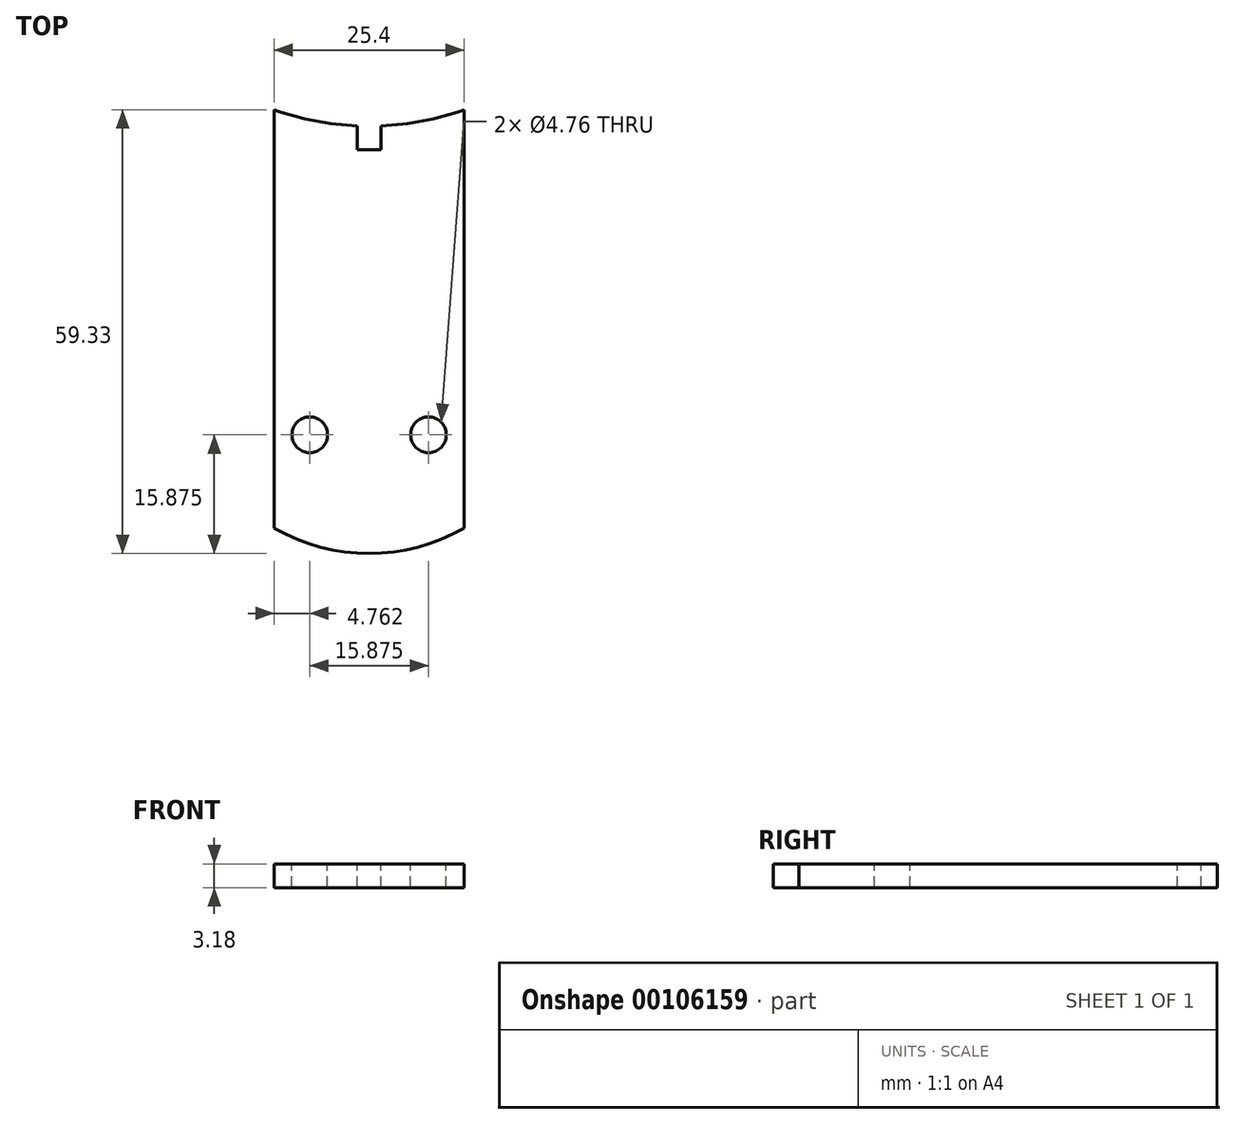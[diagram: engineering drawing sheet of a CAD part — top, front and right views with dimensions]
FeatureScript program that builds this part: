
annotation { "Feature Type Name" : "Feature", "Feature Type Description" : "" }
export const myFeature = defineFeature(function(context is Context, id is Id, definition is map)
    precondition{}
    {
        {
            var Q0;
            Q0=qCreatedBy(makeId("Top.planeOp"),FACE);
            var sketch = newSketch(context, id + "F0", { "sketchPlane" : qUnion([Q0])});
            skLineSegment(sketch, "E0.left", {"start": v(12.7, 47.4) * mm, "end": v(12.7, -47.4) * mm});
            skLineSegment(sketch, "E0.right", {"start": v(-12.7, 47.4) * mm, "end": v(-12.7, -47.4) * mm});
            skPoint(sketch, "E0.middle", {"position": v(0, 0) * mm});
            skLineSegment(sketch, "E1", {"start": v(0, -25.4) * mm, "end": v(0, 25.4) * mm});
            skArc(sketch, "E2", {"start": v(-12.7, -47.4) * mm, "mid": v(0, -50.8) * mm, "end": v(12.7, -47.4) * mm});
            skArc(sketch, "E3.trimOffspring", {"start": v(12.7, 47.4) * mm, "mid": v(0, 50.8) * mm, "end": v(-12.7, 47.4) * mm});
            skPoint(sketch, "E4", {"position": v(0, 50.8) * mm});
            skPoint(sketch, "E5", {"position": v(0, -50.8) * mm});
            skLineSegment(sketch, "E6", {"start": v(-12.7, 0) * mm, "end": v(12.7, 0) * mm});
            skSolve(sketch);
        }
        {
            var Q0;
            Q0=qSketchRegion(id+"F0",true);
            extrude(context, id + "F1", {"entities" : qUnion([Q0]), "depth" : 3.17 * mm});
        }
        {
            var Q0;
            Q0=makeQuery(id+"F1.opExtrude","CAP_FACE",FACE,{"disambiguationData":[OSD([sQuery(id+"F0.wireOp",EDGE,"E0.left"),sQuery(id+"F0.wireOp",EDGE,"E0.right"),sQuery(id+"F0.wireOp",EDGE,"E2"),sQuery(id+"F0.wireOp",EDGE,"E3.trimOffspring")])],"isStart":false});
            var sketch = newSketch(context, id + "F2", { "sketchPlane" : qUnion([Q0])});
            skLineSegment(sketch, "E7.bottom", {"start": v(7.94, 41.27) * mm, "end": v(-7.94, 41.27) * mm, "construction": true});
            skLineSegment(sketch, "E7.top", {"start": v(7.94, -34.92) * mm, "end": v(-7.94, -34.92) * mm, "construction": true});
            skLineSegment(sketch, "E7.left", {"start": v(7.94, 41.27) * mm, "end": v(7.94, -34.92) * mm, "construction": true});
            skLineSegment(sketch, "E7.right", {"start": v(-7.94, 41.27) * mm, "end": v(-7.94, -34.92) * mm, "construction": true});
            skPoint(sketch, "E7.middle", {"position": v(0, 3.18) * mm});
            skCircle(sketch, "E8", {"center": v(-7.94, 41.27) * mm, "radius": 2.38 * mm});
            skCircle(sketch, "E9", {"center": v(7.94, 41.27) * mm, "radius": 2.38 * mm});
            skCircle(sketch, "E10", {"center": v(-7.94, -34.92) * mm, "radius": 2.38 * mm});
            skCircle(sketch, "E11", {"center": v(7.94, -34.92) * mm, "radius": 2.38 * mm});
            skLineSegment(sketch, "E12", {"start": v(0, 0) * mm, "end": v(0, 3.18) * mm});
            skSolve(sketch);
        }
        {
            var Q0;
            Q0=qSketchRegion(id+"F2",true);
            extrude(context, id + "F3", {"entities" : qUnion([Q0]), "operationType" : NewBodyOperationType.REMOVE, "endBound" : BoundingType.UP_TO_NEXT, "oppositeDirection" : true, "depth" : 25.4 * mm});
        }
        {
            var Q0;
            Q0=makeQuery(id+"F1.opExtrude","CAP_FACE",FACE,{"disambiguationData":[OSD([sQuery(id+"F0.wireOp",EDGE,"E0.left"),sQuery(id+"F0.wireOp",EDGE,"E0.right"),sQuery(id+"F0.wireOp",EDGE,"E2"),sQuery(id+"F0.wireOp",EDGE,"E3.trimOffspring")])],"isStart":false});
            var sketch = newSketch(context, id + "F4", { "sketchPlane" : qUnion([Q0])});
            skPoint(sketch, "E13", {"position": v(0, 44.45) * mm});
            skPoint(sketch, "E13.positionSnap0", {"position": v(0, 50.8) * mm});
            skLineSegment(sketch, "E14", {"start": v(0, 0) * mm, "end": v(0, 25.4) * mm, "construction": true});
            skCircle(sketch, "E15", {"center": v(0, 25.4) * mm, "radius": 7.62 * mm, "construction": true});
            skCircle(sketch, "E16", {"center": v(0, 44.45) * mm, "radius": 38.1 * mm});
            skPoint(sketch, "E17", {"position": v(0, 12.7) * mm});
            skLineSegment(sketch, "E18.bottom", {"start": v(-1.59, 6.38) * mm, "end": v(1.59, 6.38) * mm});
            skLineSegment(sketch, "E18.top", {"start": v(-1.59, 3.2) * mm, "end": v(1.59, 3.2) * mm});
            skLineSegment(sketch, "E18.left", {"start": v(-1.59, 6.38) * mm, "end": v(-1.59, 3.2) * mm});
            skLineSegment(sketch, "E18.right", {"start": v(1.59, 6.38) * mm, "end": v(1.59, 3.2) * mm});
            skSolve(sketch);
        }
        {
            var Q0;
            Q0 = qSketchRegion(id + "F4", true);
            extrude(context, id + "F5", {"entities" : qUnion([Q0]), "operationType" : NewBodyOperationType.REMOVE, "endBound" : BoundingType.UP_TO_NEXT, "oppositeDirection" : true, "depth" : 25.4 * mm});
        }
    });
